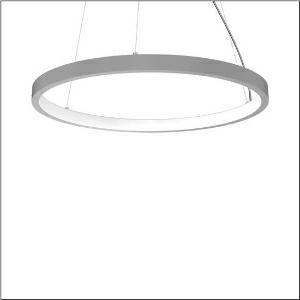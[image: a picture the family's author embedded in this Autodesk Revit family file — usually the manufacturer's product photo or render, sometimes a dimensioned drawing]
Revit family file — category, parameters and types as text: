
# Revit family: silica_21_ring-i_5pjbi4d1204a
name_source: partatom
category: Lighting Fixtures
units: mm (PartAtom-declared; Revit-internal decimal feet)

## family parameters
Cut with Voids When Loaded = No
Host = Face
Light Source = No
Part Type = Normal
Room Calculation Point = No
Round Connector Dimension = Use Diameter
Shared = No

## types (1)
- Silica 21 Ring-I (1 x LED, 8460 lm, 140 W, 3000K)
    Apparent Load = 140 VA
    CIE Flux Codes = 22 48 76 50 101
    Color Rendering = 80
    Color Temperature = 3000K
    Default Elevation = 1800 mm
    Description = Silica 21 Ring-I, suspended luminaire, of PMMA, frosted, light emission: inner ring side luminous distribution, primary light characteristic: symmetric, installation type: suspended mounting, LED, rated luminous flux: 8.460lm, luminous efficacy: 61lm/W, light colour: 830, colour temperature: 3000K, control gear: DALI 2, with terminal, 5-pole, mains connection: 230V, AC/DC, 0/50..60Hz, rated input power: 140W, housing, of extruded aluminium section, metallic grey (RAL 9006), diameter: 1.470mm, ceiling canopy, metallic grey (RAL 9006), protection rating (lamp compartment): IP40, insulation class (complete): insulation class I (protective earthing), certification: CE, impact resistance: IK02, permissible operating ambient temperature: 0..+35°C, packaging unit: 1 piece
    Height = 48 mm
    Lamp = 1 x LED
    Lamp Light Flux = 8460 lm
    Lamp Power = 140 W
    Lamp count = 1
    Length = 1470 mm
    Luminous efficacy = 60 lm/W
    Manufacturer = Siteco
    ModVariant = No
    Model = 5PJBI4D1204A
    Mounting Place = Ceiling
    Mounting Type = Pendant
    Number of Poles = 1
    OnlyDefault = Yes
    Power Factor = 1
    Product Name = Silica 21 Ring-I
    Product group = suspended luminaire
    ProductGroupID = 904
    Protection Class = Protection class I
    Protection Degree = IP 40
    RLX_Detail_Level = 1
    RLX_Emergency_Light_Flux = 0 lm
    RLX_Emergency_Type = 0
    RLX_Emergency_Type_DB = No
    RlxData = <blob elided: 18837 chars, md5=7f46b66b>
    Socket = socket
    Standby Power = 0 W
    System Light Flux = 8460 lm
    System Power = 140 W
    Type Comments = Product without accessories
    Type Image = l_1251756.jpg
    URL = http://relux.com
    VarID = ---
    Voltage = 0 V
    Weight = 0.00 kg
    Width = 0 mm  [stored 0 ft]

note: [stored X ft] marks values corroborated as IEEE doubles in the binary element streams (Revit-internal decimal feet)

## geometry (parser evidence)
native form markers: Blend x4, Sweep x14
no freeform markers — native parametric forms only
